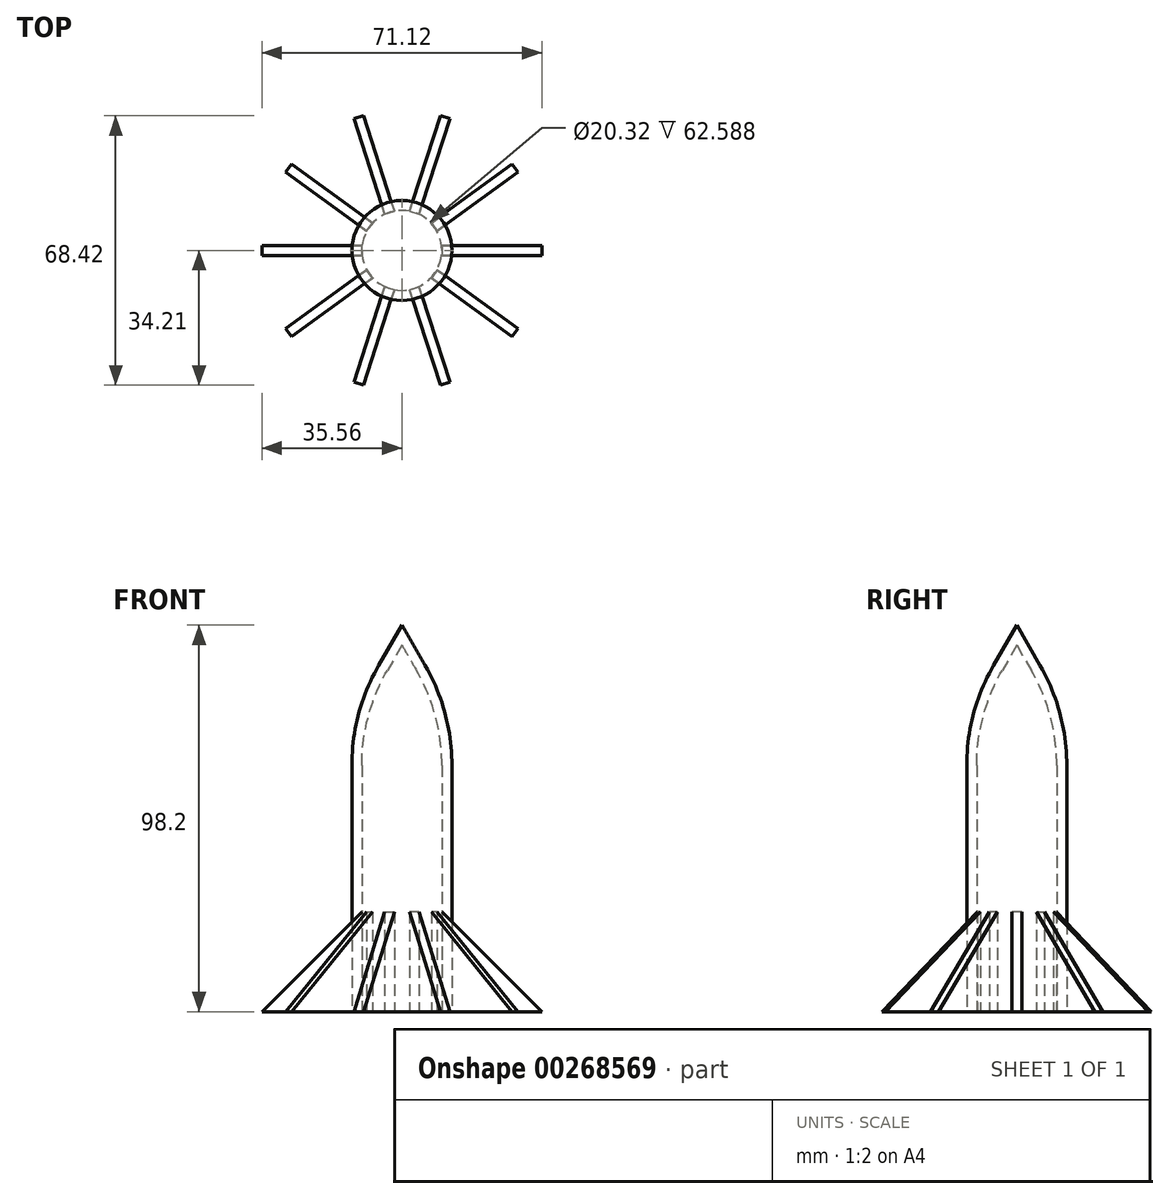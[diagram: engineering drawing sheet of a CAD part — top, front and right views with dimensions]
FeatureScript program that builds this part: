
annotation { "Feature Type Name" : "Feature", "Feature Type Description" : "" }
export const myFeature = defineFeature(function(context is Context, id is Id, definition is map)
    precondition{}
    {
        {
            var Q0;
            Q0=qCreatedBy(makeId("Top.planeOp"),FACE);
            var sketch = newSketch(context, id + "F0", { "sketchPlane" : qUnion([Q0])});
            skCircle(sketch, "E0", {"center": v(0, 0) * mm, "radius": 12.7 * mm});
            skSolve(sketch);
        }
        {
            var Q0;
            Q0 = qSketchRegion(id + "F0", true);
            extrude(context, id + "F1", {"entities" : qUnion([Q0]), "depth" : 76.2 * mm});
        }
        {
            var Q0;
            Q0=makeQuery(id+"F1.opExtrude","CAP_FACE",FACE,{"disambiguationData":[OSD([sQuery(id+"F0.wireOp",EDGE,"E0")])],"isStart":false});
            extrude(context, id + "F2", {"entities" : qUnion([Q0]), "operationType" : NewBodyOperationType.ADD, "depth" : 25.4 * mm, "hasDraft" : true, "draftAngle" : 30 * degree, "draftPullDirection" : true});
        }
        {
            var Q0;
            {var subQ0=sQuery(id+"F0.wireOp",EDGE,"E0");Q0=makeQuery(id+"F2.boolean.opBoolean","MERGE",EDGE,{"derivedFrom":[makeQuery(id+"F1.opExtrude","CAP_EDGE",EDGE,{"disambiguationData":[OSD([subQ0])],"isStart":false}),makeQuery(id+"F2.opExtrude","CAP_EDGE",EDGE,{"disambiguationData":[OSD([subQ0])],"isStart":true})]});}
            fillet(context, id + "F3", {"entities" : qUnion([Q0]), "radius" : 50.8 * mm, "tangentPropagation" : true, "allowEdgeOverflow" : false});
        }
        {
            var Q0;
            Q0=makeQuery(id+"F1.opExtrude","CAP_FACE",FACE,{"disambiguationData":[OSD([sQuery(id+"F0.wireOp",EDGE,"E0")])],"isStart":true});
            shell(context, id + "F4", {"entities" : qUnion([Q0]), "thickness" : 2.54 * mm});
        }
        {
            var Q0;
            Q0=qCreatedBy(makeId("Front.planeOp"),FACE);
            var sketch = newSketch(context, id + "F5", { "sketchPlane" : qUnion([Q0])});
            skLineSegment(sketch, "E1", {"start": v(-10.16, 0) * mm, "end": v(-35.56, 0) * mm});
            skLineSegment(sketch, "E2", {"start": v(-35.56, 0) * mm, "end": v(-10.16, 25.4) * mm});
            skLineSegment(sketch, "E3", {"start": v(-10.16, 25.4) * mm, "end": v(-10.16, 0) * mm});
            skSolve(sketch);
        }
        {
            var Q0;
            Q0 = qSketchRegion(id + "F5", true);
            extrude(context, id + "F6", {"entities" : qUnion([Q0]), "endBound" : BoundingType.SYMMETRIC, "depth" : 2.54 * mm});
        }
        {
            var Q0;
            Q0=makeQuery(id+"F6.opExtrude","SWEPT_BODY",BODY,{"disambiguationData":[OSD([sQuery(id+"F5.wireOp",EDGE,"E1"),sQuery(id+"F5.wireOp",EDGE,"E2"),sQuery(id+"F5.wireOp",EDGE,"E3")])]});
            var Q1;
            {var subQ0=sQuery(id+"F0.wireOp",EDGE,"E0");Q1=makeQuery(id+"F4.opShell","OFFSET_EDGE",EDGE,{"disambiguationData":[OSD([subQ0]),TDD([makeQuery(id+"F1.opExtrude","CAP_EDGE",EDGE,{"disambiguationData":[OSD([subQ0])],"isStart":true})])]});}
            circularPattern(context, id + "F7", {"entities" : qUnion([Q0]), "axis" : qUnion([Q1]), "angle" : 360 * degree, "instanceCount" : 10, "equalSpace" : true});
        }
    });
